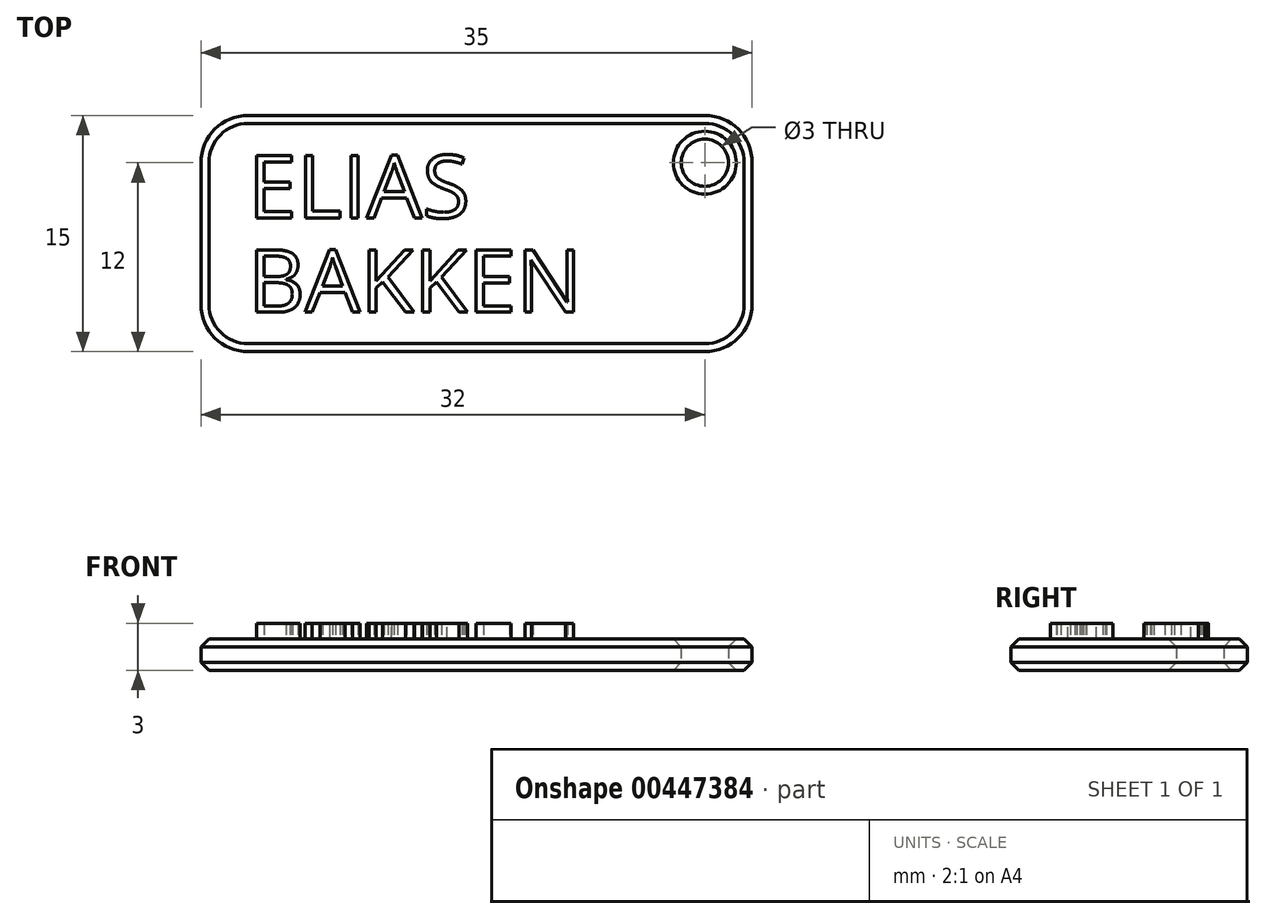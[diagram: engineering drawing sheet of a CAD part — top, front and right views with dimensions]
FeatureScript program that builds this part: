
annotation { "Feature Type Name" : "Feature", "Feature Type Description" : "" }
export const myFeature = defineFeature(function(context is Context, id is Id, definition is map)
    precondition{}
    {
        {
            var Q0;
            Q0=qCreatedBy(makeId("Top.planeOp"),FACE);
            var sketch = newSketch(context, id + "F0", { "sketchPlane" : qUnion([Q0])});
            skLineSegment(sketch, "E0.bottom", {"start": v(17.5, -7.5) * mm, "end": v(-17.5, -7.5) * mm});
            skLineSegment(sketch, "E0.top", {"start": v(17.5, 7.5) * mm, "end": v(-17.5, 7.5) * mm});
            skLineSegment(sketch, "E0.left", {"start": v(17.5, -7.5) * mm, "end": v(17.5, 7.5) * mm});
            skLineSegment(sketch, "E0.right", {"start": v(-17.5, -7.5) * mm, "end": v(-17.5, 7.5) * mm});
            skPoint(sketch, "E0.middle", {"position": v(0, 0) * mm});
            skCircle(sketch, "E1", {"center": v(14.5, 4.5) * mm, "radius": 1.5 * mm});
            skSolve(sketch);
        }
        {
            var Q0;
            Q0=makeQuery(id+"F0.imprint","IMPRINT",FACE,{"disambiguationData":[TD([[makeQuery(id+"F0.imprint","IMPRINT",EDGE,{"derivedFrom":sQuery(id+"F0.wireOp",EDGE,"E0.bottom")}),-1.0]])]});
            extrude(context, id + "F1", {"entities" : qUnion([Q0]), "depth" : 2 * mm});
        }
        {
            var Q0;
            Q0=makeQuery(id+"F1.opExtrude","SWEPT_EDGE",EDGE,{"disambiguationData":[OSD([sQuery(id+"F0.wireOp",EDGE,"E0.top"),sQuery(id+"F0.wireOp",EDGE,"E0.right")])]});
            var Q1;
            Q1=makeQuery(id+"F1.opExtrude","SWEPT_EDGE",EDGE,{"disambiguationData":[OSD([sQuery(id+"F0.wireOp",EDGE,"E0.bottom"),sQuery(id+"F0.wireOp",EDGE,"E0.right")])]});
            var Q2;
            Q2=makeQuery(id+"F1.opExtrude","SWEPT_EDGE",EDGE,{"disambiguationData":[OSD([sQuery(id+"F0.wireOp",EDGE,"E0.bottom"),sQuery(id+"F0.wireOp",EDGE,"E0.left")])]});
            var Q3;
            Q3=makeQuery(id+"F1.opExtrude","SWEPT_EDGE",EDGE,{"disambiguationData":[OSD([sQuery(id+"F0.wireOp",EDGE,"E0.top"),sQuery(id+"F0.wireOp",EDGE,"E0.left")])]});
            fillet(context, id + "F2", {"entities" : qUnion([Q0, Q1, Q2, Q3]), "radius" : 3 * mm, "tangentPropagation" : true, "allowEdgeOverflow" : false});
        }
        {
            var Q0;
            Q0=makeQuery(id+"F1.opExtrude","CAP_FACE",FACE,{"disambiguationData":[OSD([sQuery(id+"F0.wireOp",EDGE,"E0.bottom"),sQuery(id+"F0.wireOp",EDGE,"E0.top"),sQuery(id+"F0.wireOp",EDGE,"E0.left"),sQuery(id+"F0.wireOp",EDGE,"E0.right"),sQuery(id+"F0.wireOp",EDGE,"E1")])],"isStart":false});
            var sketch = newSketch(context, id + "F3", { "sketchPlane" : qUnion([Q0])});
            skText(sketch, "E2", { "text": "ELIAS", "fontName": "OpenSans-Regular.ttf"});
            skText(sketch, "E3", { "text": "BAKKEN", "fontName": "OpenSans-Regular.ttf"});
            const initialGuessF3  = {"E2": [-0.0145, 0.001, 1, 0, 0.004], "E3": [-0.0145, -0.005, 1, 0, 0.004]};
            skSetInitialGuess(sketch, initialGuessF3);
            skSolve(sketch);
        }
        {
            var Q0;
            Q0 = qSketchRegion(id + "F3", true);
            extrude(context, id + "F4", {"entities" : qUnion([Q0]), "operationType" : NewBodyOperationType.ADD, "depth" : 1 * mm});
        }
        {
            var Q0;
            Q0=makeQuery(id+"F1.opExtrude","SWEPT_FACE",FACE,{"disambiguationData":[OSD([sQuery(id+"F0.wireOp",EDGE,"E1")])]});
            chamfer(context, id + "F5", {"entities" : qUnion([Q0]), "width" : 0.5 * mm, "tangentPropagation" : true});
        }
        {
            var Q0;
            Q0=makeQuery(id+"F1.opExtrude","SWEPT_FACE",FACE,{"disambiguationData":[OSD([sQuery(id+"F0.wireOp",EDGE,"E0.top")])]});
            chamfer(context, id + "F6", {"entities" : qUnion([Q0]), "width" : 0.5 * mm, "tangentPropagation" : true});
        }
    });
